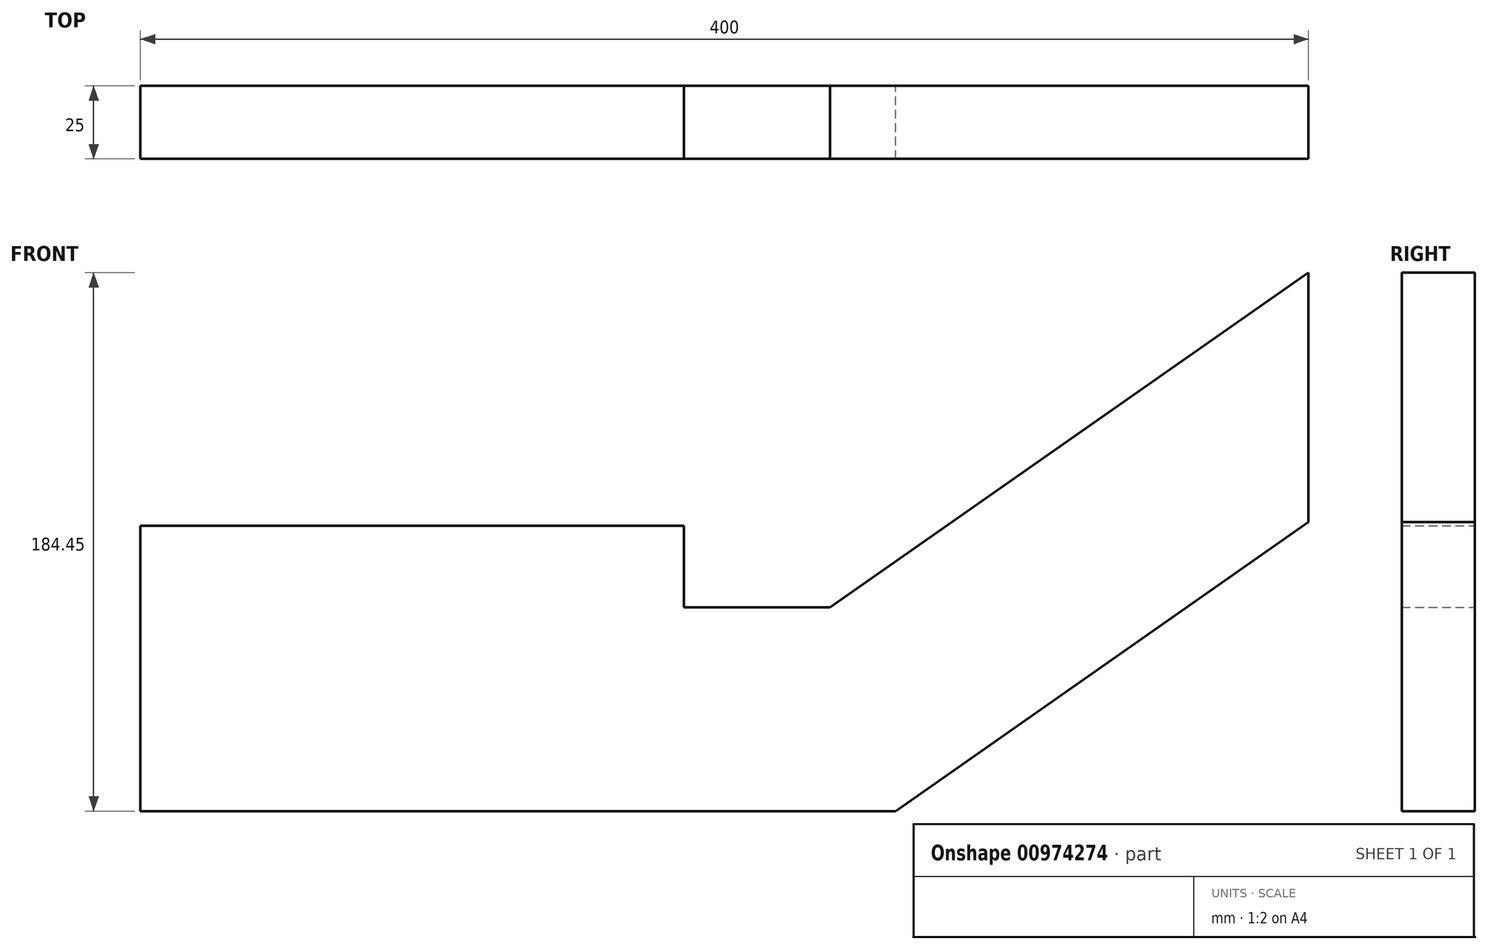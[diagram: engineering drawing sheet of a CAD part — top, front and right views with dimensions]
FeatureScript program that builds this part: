
annotation { "Feature Type Name" : "Feature", "Feature Type Description" : "" }
export const myFeature = defineFeature(function(context is Context, id is Id, definition is map)
    precondition{}
    {
        {
            var Q0;
            Q0=qCreatedBy(makeId("Front.planeOp"),FACE);
            var sketch = newSketch(context, id + "F0", { "sketchPlane" : qUnion([Q0])});
            skLineSegment(sketch, "E0.bottom", {"start": v(0, 0) * mm, "end": v(258.61, 0) * mm});
            skLineSegment(sketch, "E0.left", {"start": v(0, 0) * mm, "end": v(0, 97.74) * mm});
            skLineSegment(sketch, "E0.right", {"start": v(400, 99) * mm, "end": v(400, 184.45) * mm});
            skLineSegment(sketch, "E1", {"start": v(0, 97.74) * mm, "end": v(186.17, 97.74) * mm});
            skLineSegment(sketch, "E2", {"start": v(186.17, 97.74) * mm, "end": v(186.17, 69.74) * mm});
            skLineSegment(sketch, "E3", {"start": v(186.17, 69.74) * mm, "end": v(236.17, 69.74) * mm});
            skLineSegment(sketch, "E4", {"start": v(236.17, 69.74) * mm, "end": v(400, 184.45) * mm});
            skLineSegment(sketch, "E5", {"start": v(400, 99) * mm, "end": v(258.61, 0) * mm});
            skSolve(sketch);
        }
        {
            var Q0;
            Q0 = qSketchRegion(id + "F0", true);
            extrude(context, id + "F1", {"entities" : qUnion([Q0]), "depth" : 25 * mm, "offsetDistance" : 25 * mm});
        }
    });
